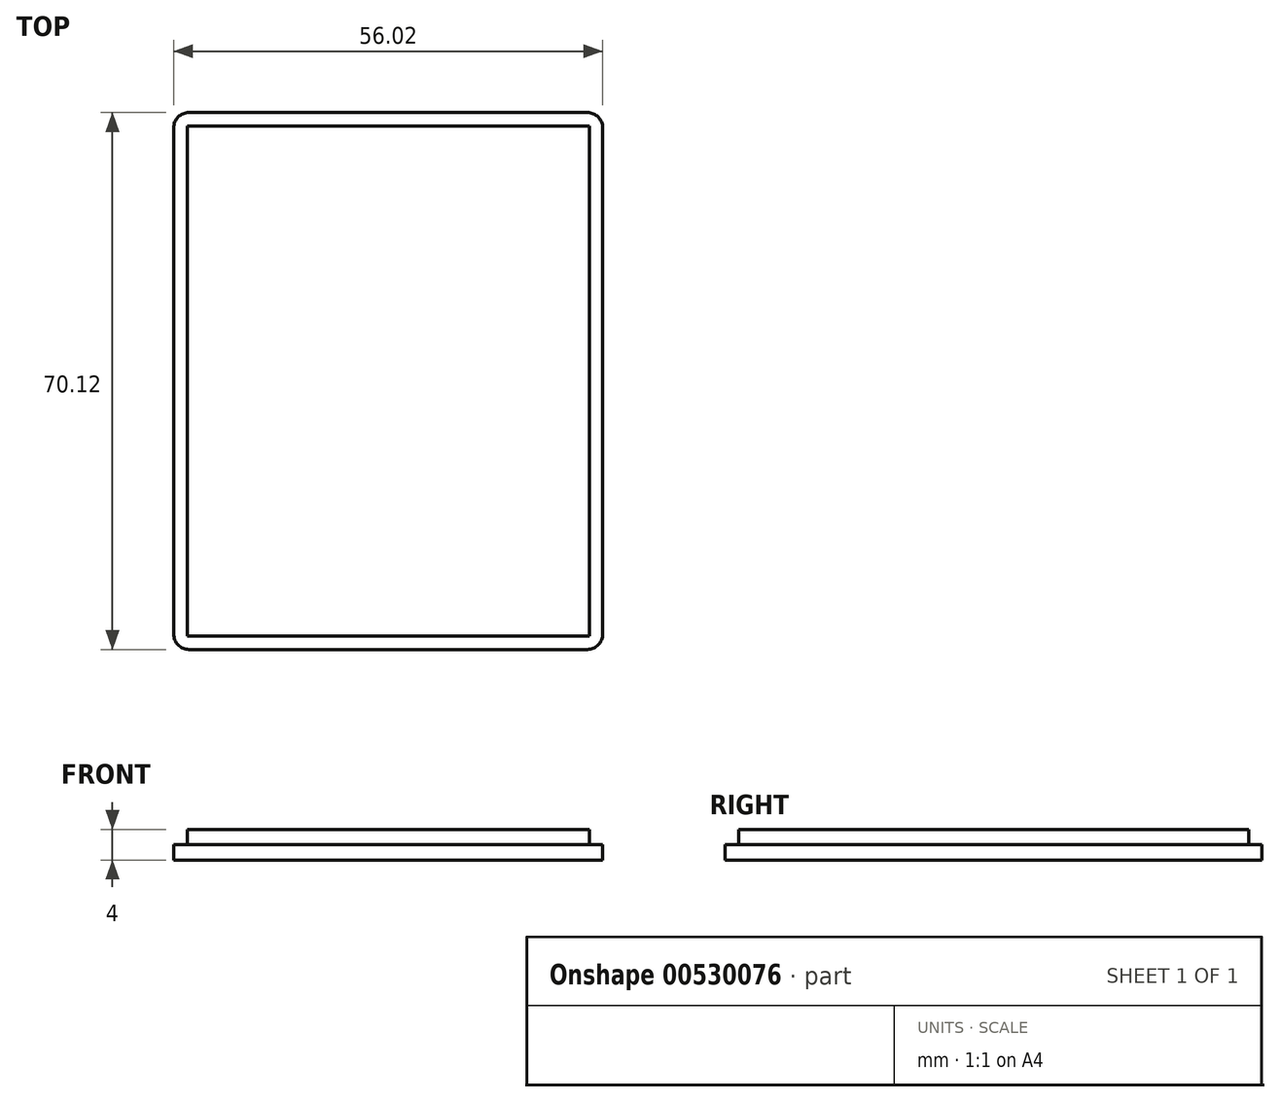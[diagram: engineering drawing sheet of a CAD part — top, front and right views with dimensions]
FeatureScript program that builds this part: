
annotation { "Feature Type Name" : "Feature", "Feature Type Description" : "" }
export const myFeature = defineFeature(function(context is Context, id is Id, definition is map)
    precondition{}
    {
        {
            var Q0;
            Q0=qCreatedBy(makeId("Top.planeOp"),FACE);
            var sketch = newSketch(context, id + "F0", { "sketchPlane" : qUnion([Q0])});
            skLineSegment(sketch, "E0", {"start": v(-37.78, -30.92) * mm, "end": v(-37.78, 39.2) * mm});
            skLineSegment(sketch, "E1", {"start": v(-37.78, 39.2) * mm, "end": v(18.24, 39.2) * mm});
            skLineSegment(sketch, "E2", {"start": v(18.24, 39.2) * mm, "end": v(18.24, -30.92) * mm});
            skLineSegment(sketch, "E3", {"start": v(18.24, -30.92) * mm, "end": v(-37.78, -30.92) * mm});
            skLineSegment(sketch, "E4", {"start": v(16.49, 37.45) * mm, "end": v(-36.03, 37.45) * mm});
            skLineSegment(sketch, "E5", {"start": v(-36.03, 37.45) * mm, "end": v(-36.03, -29.17) * mm});
            skLineSegment(sketch, "E6", {"start": v(-36.03, -29.17) * mm, "end": v(16.49, -29.17) * mm});
            skLineSegment(sketch, "E7", {"start": v(16.49, -29.17) * mm, "end": v(16.49, 37.45) * mm});
            skSolve(sketch);
        }
        {
            var Q0;
            Q0=makeQuery(id+"F0.imprint","IMPRINT",FACE,{"disambiguationData":[TD([[makeQuery(id+"F0.imprint","IMPRINT",EDGE,{"derivedFrom":sQuery(id+"F0.wireOp",EDGE,"E0")}),-1.0]])]});
            extrude(context, id + "F1", {"entities" : qUnion([Q0]), "depth" : 2 * mm, "offsetDistance" : 25 * mm});
        }
        {
            var Q0;
            Q0=makeQuery(id+"F1.opExtrude","SWEPT_EDGE",EDGE,{"disambiguationData":[OSD([sQuery(id+"F0.wireOp",EDGE,"E0"),sQuery(id+"F0.wireOp",EDGE,"E3")])]});
            var Q1;
            Q1=makeQuery(id+"F1.opExtrude","SWEPT_EDGE",EDGE,{"disambiguationData":[OSD([sQuery(id+"F0.wireOp",EDGE,"E0"),sQuery(id+"F0.wireOp",EDGE,"E1")])]});
            var Q2;
            Q2=makeQuery(id+"F1.opExtrude","SWEPT_EDGE",EDGE,{"disambiguationData":[OSD([sQuery(id+"F0.wireOp",EDGE,"E1"),sQuery(id+"F0.wireOp",EDGE,"E2")])]});
            var Q3;
            Q3=makeQuery(id+"F1.opExtrude","SWEPT_EDGE",EDGE,{"disambiguationData":[OSD([sQuery(id+"F0.wireOp",EDGE,"E2"),sQuery(id+"F0.wireOp",EDGE,"E3")])]});
            fillet(context, id + "F2", {"entities" : qUnion([Q0, Q1, Q2, Q3]), "radius" : 2 * mm, "tangentPropagation" : true, "allowEdgeOverflow" : false});
        }
        {
            var Q0;
            Q0=makeQuery(id+"F0.imprint","IMPRINT",FACE,{"disambiguationData":[TD([[makeQuery(id+"F0.imprint","IMPRINT",EDGE,{"derivedFrom":sQuery(id+"F0.wireOp",EDGE,"E4")}),1.0]])]});
            extrude(context, id + "F3", {"entities" : qUnion([Q0]), "operationType" : NewBodyOperationType.ADD, "depth" : 4 * mm, "offsetDistance" : 25 * mm});
        }
    });
